# Revit family: CXR
name_source: partatom
category: Communication Devices
revit_build: Autodesk Revit 2014 (Build: 20130308_1515(x64)
units: mm (PartAtom-declared; Revit-internal decimal feet)

## types (1)
- CXR
    Assembly Code = D5090
    Black Element = Metal-Hubbell-Nickel
    Blue Element = Metal-Hubbell-Aluminum Anodized Blue
    Certification = This product qualifies as “designated country
construction material” per FAR 52.225-11 Buy
American-Construction Materials under Trade
Agreements effective 5/27/2020.
    Default Elevation = 48 "
    Description = CX Relay
    Features = Relays are mounted to individual relay cards
• Four types of relays - 20A/1P, N/O and 20A/2P, N/O, N/C (14K SCCR) and
30A 1P latching (18K SCCR)
• Smart Relay card self-identifies type automatically to panel
• Each relay includes 1 programmable input for low voltage switches,
photocells or motion sensors
• Relay cards include a manual override control button and LED
status indication
    Housing Material = Paint - Hubbell - Matte White
    Inrush Withstand = CXR2N 120/277VAC (50/60Hz)
• CXR3L 120/277/347VAC (50/60Hz)
• CXR3LEM 120/277/347VAC (50/60Hz)
• CXRTN 208/240/480VAC (50/60Hz)
• CXRTC 208/240/480VAC (50/60Hz)
• CX04/CX08; 24VDC, 150mA (max. 300mA)
• CX16/CX24; 24VDC, 150mA (max. 900mA)
• 500A @ 2ms (CXR3LEM only)
    Manufacturer = Hubbell Control Solutions
    Model = CX Relays
    Operating environment = Location: interior space
Operating temperature: 0°- 50°C (32° - 112°F)
Relative humidity (non-condensing): 10%-90%
    Product Documentation URL = https://hubbellcdn.com
    Product Page URL = https://www.hubbell.com
    Type Comments = NX Panel Relay
    URL = https://www.hubbell.com
    Warranty = 5-Years Warranty

## geometry (parser evidence)
native form markers: Sweep x1
no freeform markers — native parametric forms only
